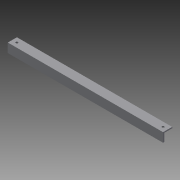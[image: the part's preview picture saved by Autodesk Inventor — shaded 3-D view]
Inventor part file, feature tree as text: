
AUTODESK INVENTOR PART (.ipt)
format: ipt  version: 2015 SP1 (Build 190203100, 203)  size: 84,992 bytes
history: native  units: in
note: dims shown in document units (in); Inventor stores cm internally (conversion verified against a paired STEP export)
features: sketch x2, extrude x1, hole x1
ambient origin geometry x8: Origin, YZ Plane, XZ Plane, XY Plane, X Axis, Y Axis, Z Axis, Center Point
bodies: Solid1 (feature_tree)
feature tree (4):
  extrude  "Extrusion1"  Depth=1.0in
  hole  "Hole1"  [1 undecoded]
  sketch  "Sketch1"  dims[d0=0.125in d1=1.0in]
  sketch  "Sketch2"  dims[d2=1.0in d3=0.125in d4=21.5in d5=0.0in d6=2.75in d7=0.5in d8=2.75in d9=0.5in d10=0.25in d11=0.75in d12=0.375in d13=0.25in d14=0.5635in d15=1.0in d16=0.8108in]
note: 1 required parameter value undecoded (feature->parameter linkage not recoverable at this tier; creation-order binding heuristic only, values carry confidence <= 0.55)
